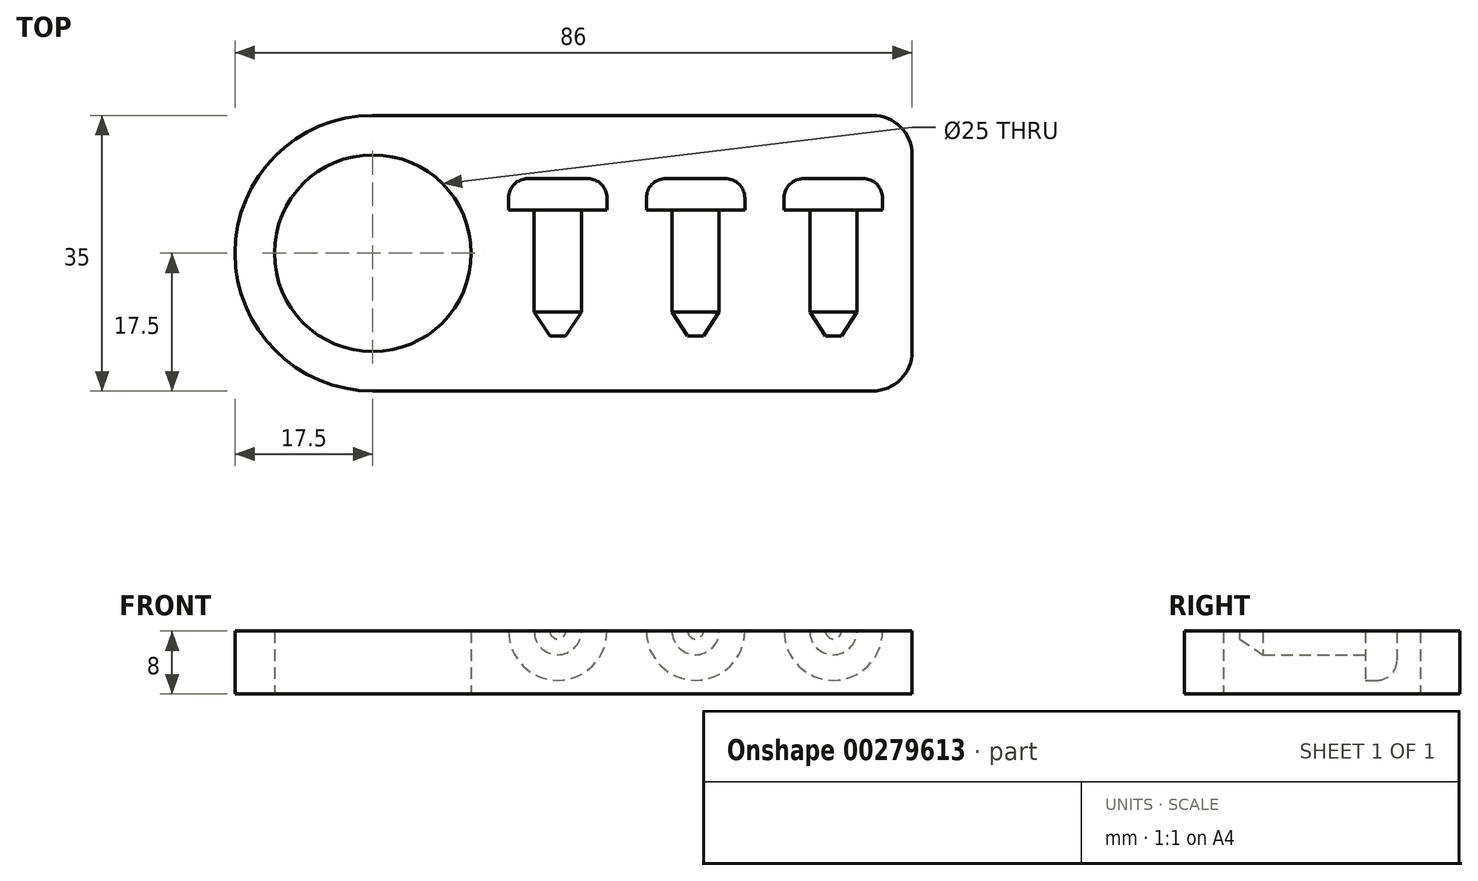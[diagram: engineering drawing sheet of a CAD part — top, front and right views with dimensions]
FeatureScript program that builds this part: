
annotation { "Feature Type Name" : "Feature", "Feature Type Description" : "" }
export const myFeature = defineFeature(function(context is Context, id is Id, definition is map)
    precondition{}
    {
        {
            var Q0;
            Q0=qCreatedBy(makeId("Top.planeOp"),FACE);
            var sketch = newSketch(context, id + "F0", { "sketchPlane" : qUnion([Q0])});
            skLineSegment(sketch, "E0.bottom", {"start": v(17.5, 0) * mm, "end": v(81, 0) * mm});
            skLineSegment(sketch, "E0.top", {"start": v(17.5, 35) * mm, "end": v(81, 35) * mm});
            skLineSegment(sketch, "E0.left", {"start": v(0, 17.5) * mm, "end": v(0, 17.5) * mm});
            skLineSegment(sketch, "E0.right", {"start": v(86, 5) * mm, "end": v(86, 30) * mm});
            skLineSegment(sketch, "E1.bottom", {"start": v(0, 0) * mm, "end": v(17.5, 0) * mm, "construction": true});
            skLineSegment(sketch, "E1.top", {"start": v(0, 17.5) * mm, "end": v(17.5, 17.5) * mm, "construction": true});
            skLineSegment(sketch, "E1.left", {"start": v(0, 0) * mm, "end": v(0, 17.5) * mm, "construction": true});
            skLineSegment(sketch, "E1.right", {"start": v(17.5, 0) * mm, "end": v(17.5, 17.5) * mm, "construction": true});
            skCircle(sketch, "E2", {"center": v(17.5, 17.5) * mm, "radius": 12.5 * mm});
            skPoint(sketch, "E3.visualSharp", {"position": v(0, 0) * mm});
            skArc(sketch, "E3.filletArc", {"start": v(0, 17.5) * mm, "mid": v(5.13, 5.13) * mm, "end": v(17.5, 0) * mm});
            skPoint(sketch, "E4.visualSharp", {"position": v(0, 35) * mm});
            skArc(sketch, "E4.filletArc", {"start": v(17.5, 35) * mm, "mid": v(5.13, 29.87) * mm, "end": v(0, 17.5) * mm});
            skPoint(sketch, "E5.visualSharp", {"position": v(86, 35) * mm});
            skArc(sketch, "E5.filletArc", {"start": v(86, 30) * mm, "mid": v(84.54, 33.54) * mm, "end": v(81, 35) * mm});
            skPoint(sketch, "E6.visualSharp", {"position": v(86, 0) * mm});
            skArc(sketch, "E6.filletArc", {"start": v(81, 0) * mm, "mid": v(84.54, 1.46) * mm, "end": v(86, 5) * mm});
            skSolve(sketch);
        }
        {
            var Q0;
            Q0=makeQuery(id+"F0.imprint","IMPRINT",FACE,{"disambiguationData":[TD([[makeQuery(id+"F0.imprint","IMPRINT",EDGE,{"derivedFrom":sQuery(id+"F0.wireOp",EDGE,"E0.bottom")}),1.0]])]});
            extrude(context, id + "F1", {"entities" : qUnion([Q0]), "depth" : 8 * mm});
        }
        {
            var Q0;
            Q0=makeQuery(id+"F1.opExtrude","CAP_FACE",FACE,{"disambiguationData":[OSD([sQuery(id+"F0.wireOp",EDGE,"E0.bottom"),sQuery(id+"F0.wireOp",EDGE,"E0.top"),sQuery(id+"F0.wireOp",EDGE,"E0.right"),sQuery(id+"F0.wireOp",EDGE,"E2"),sQuery(id+"F0.wireOp",EDGE,"E3.filletArc"),sQuery(id+"F0.wireOp",EDGE,"E4.filletArc"),sQuery(id+"F0.wireOp",EDGE,"E5.filletArc"),sQuery(id+"F0.wireOp",EDGE,"E6.filletArc")])],"isStart":false});
            var sketch = newSketch(context, id + "F2", { "sketchPlane" : qUnion([Q0])});
            skLineSegment(sketch, "E7.bottom", {"start": v(0, 0) * mm, "end": v(41, 0) * mm, "construction": true});
            skLineSegment(sketch, "E7.top", {"start": v(0, 7) * mm, "end": v(41, 7) * mm, "construction": true});
            skLineSegment(sketch, "E7.left", {"start": v(0, 0) * mm, "end": v(0, 7) * mm, "construction": true});
            skLineSegment(sketch, "E7.right", {"start": v(41, 0) * mm, "end": v(41, 7) * mm, "construction": true});
            skLineSegment(sketch, "E8", {"start": v(41, 7) * mm, "end": v(41, 23) * mm});
            skLineSegment(sketch, "E9", {"start": v(41, 7) * mm, "end": v(42, 7) * mm});
            skLineSegment(sketch, "E10.bottom", {"start": v(44, 23) * mm, "end": v(47.25, 23) * mm});
            skLineSegment(sketch, "E10.top", {"start": v(41, 27) * mm, "end": v(44.75, 27) * mm});
            skLineSegment(sketch, "E10.left", {"start": v(41, 23) * mm, "end": v(41, 27) * mm});
            skLineSegment(sketch, "E10.right", {"start": v(47.25, 23) * mm, "end": v(47.25, 24.5) * mm});
            skPoint(sketch, "E11.visualSharp", {"position": v(47.25, 27) * mm});
            skArc(sketch, "E11.filletArc", {"start": v(47.25, 24.5) * mm, "mid": v(46.52, 26.27) * mm, "end": v(44.75, 27) * mm});
            skLineSegment(sketch, "E12", {"start": v(44, 23) * mm, "end": v(44, 10) * mm});
            skLineSegment(sketch, "E13", {"start": v(44, 10) * mm, "end": v(42, 7) * mm});
            skLineSegment(sketch, "E14", {"start": v(41, 7) * mm, "end": v(58.5, 7) * mm, "construction": true});
            skLineSegment(sketch, "E15", {"start": v(58.5, 7) * mm, "end": v(76, 7) * mm, "construction": true});
            skLineSegment(sketch, "E16", {"start": v(58.5, 7) * mm, "end": v(58.5, 23) * mm});
            skLineSegment(sketch, "E17", {"start": v(58.5, 7) * mm, "end": v(59.5, 7) * mm});
            skLineSegment(sketch, "E18.bottom", {"start": v(61.5, 23) * mm, "end": v(64.75, 23) * mm});
            skLineSegment(sketch, "E18.top", {"start": v(58.5, 27) * mm, "end": v(62.25, 27) * mm});
            skLineSegment(sketch, "E18.left", {"start": v(58.5, 23) * mm, "end": v(58.5, 27) * mm});
            skLineSegment(sketch, "E18.right", {"start": v(64.75, 23) * mm, "end": v(64.75, 24.5) * mm});
            skPoint(sketch, "E19.visualSharp", {"position": v(64.75, 27) * mm});
            skArc(sketch, "E19.filletArc", {"start": v(64.75, 24.5) * mm, "mid": v(64.02, 26.27) * mm, "end": v(62.25, 27) * mm});
            skLineSegment(sketch, "E20", {"start": v(61.5, 23) * mm, "end": v(61.5, 10) * mm});
            skLineSegment(sketch, "E21", {"start": v(61.5, 10) * mm, "end": v(59.5, 7) * mm});
            skLineSegment(sketch, "E22", {"start": v(76, 7) * mm, "end": v(76, 23) * mm});
            skLineSegment(sketch, "E23", {"start": v(76, 7) * mm, "end": v(77, 7) * mm});
            skLineSegment(sketch, "E24.bottom", {"start": v(79, 23) * mm, "end": v(82.25, 23) * mm});
            skLineSegment(sketch, "E24.top", {"start": v(76, 27) * mm, "end": v(79.75, 27) * mm});
            skLineSegment(sketch, "E24.left", {"start": v(76, 23) * mm, "end": v(76, 27) * mm});
            skLineSegment(sketch, "E24.right", {"start": v(82.25, 23) * mm, "end": v(82.25, 24.5) * mm});
            skPoint(sketch, "E25.visualSharp", {"position": v(82.25, 27) * mm});
            skArc(sketch, "E25.filletArc", {"start": v(82.25, 24.5) * mm, "mid": v(81.52, 26.27) * mm, "end": v(79.75, 27) * mm});
            skLineSegment(sketch, "E26", {"start": v(79, 23) * mm, "end": v(79, 10) * mm});
            skLineSegment(sketch, "E27", {"start": v(79, 10) * mm, "end": v(77, 7) * mm});
            skSolve(sketch);
        }
        {
            var Q0;
            Q0=makeQuery(id+"F2.imprint","IMPRINT",FACE,{"disambiguationData":[TD([[makeQuery(id+"F2.imprint","IMPRINT",EDGE,{"derivedFrom":sQuery(id+"F2.wireOp",EDGE,"E8")}),-1.0]])]});
            var Q1;
            Q1=sQuery(id+"F2.wireOp",EDGE,"E8");
            revolve(context, id + "F3", {"operationType" : NewBodyOperationType.REMOVE, "entities" : qUnion([Q0]), "axis" : qUnion([Q1]), "revolveType" : RevolveType.FULL, "oppositeDirection" : true});
        }
        {
            var Q0;
            Q0=makeQuery(id+"F2.imprint","IMPRINT",FACE,{"disambiguationData":[TD([[makeQuery(id+"F2.imprint","IMPRINT",EDGE,{"derivedFrom":sQuery(id+"F2.wireOp",EDGE,"E16")}),-1.0]])]});
            var Q1;
            Q1=sQuery(id+"F2.wireOp",EDGE,"E16");
            revolve(context, id + "F4", {"operationType" : NewBodyOperationType.REMOVE, "entities" : qUnion([Q0]), "axis" : qUnion([Q1]), "revolveType" : RevolveType.FULL, "oppositeDirection" : true});
        }
        {
            var Q0;
            Q0=makeQuery(id+"F2.imprint","IMPRINT",FACE,{"disambiguationData":[TD([[makeQuery(id+"F2.imprint","IMPRINT",EDGE,{"derivedFrom":sQuery(id+"F2.wireOp",EDGE,"E22")}),-1.0]])]});
            var Q1;
            Q1=sQuery(id+"F2.wireOp",EDGE,"E22");
            revolve(context, id + "F5", {"operationType" : NewBodyOperationType.REMOVE, "entities" : qUnion([Q0]), "axis" : qUnion([Q1]), "revolveType" : RevolveType.FULL, "oppositeDirection" : true});
        }
    });
